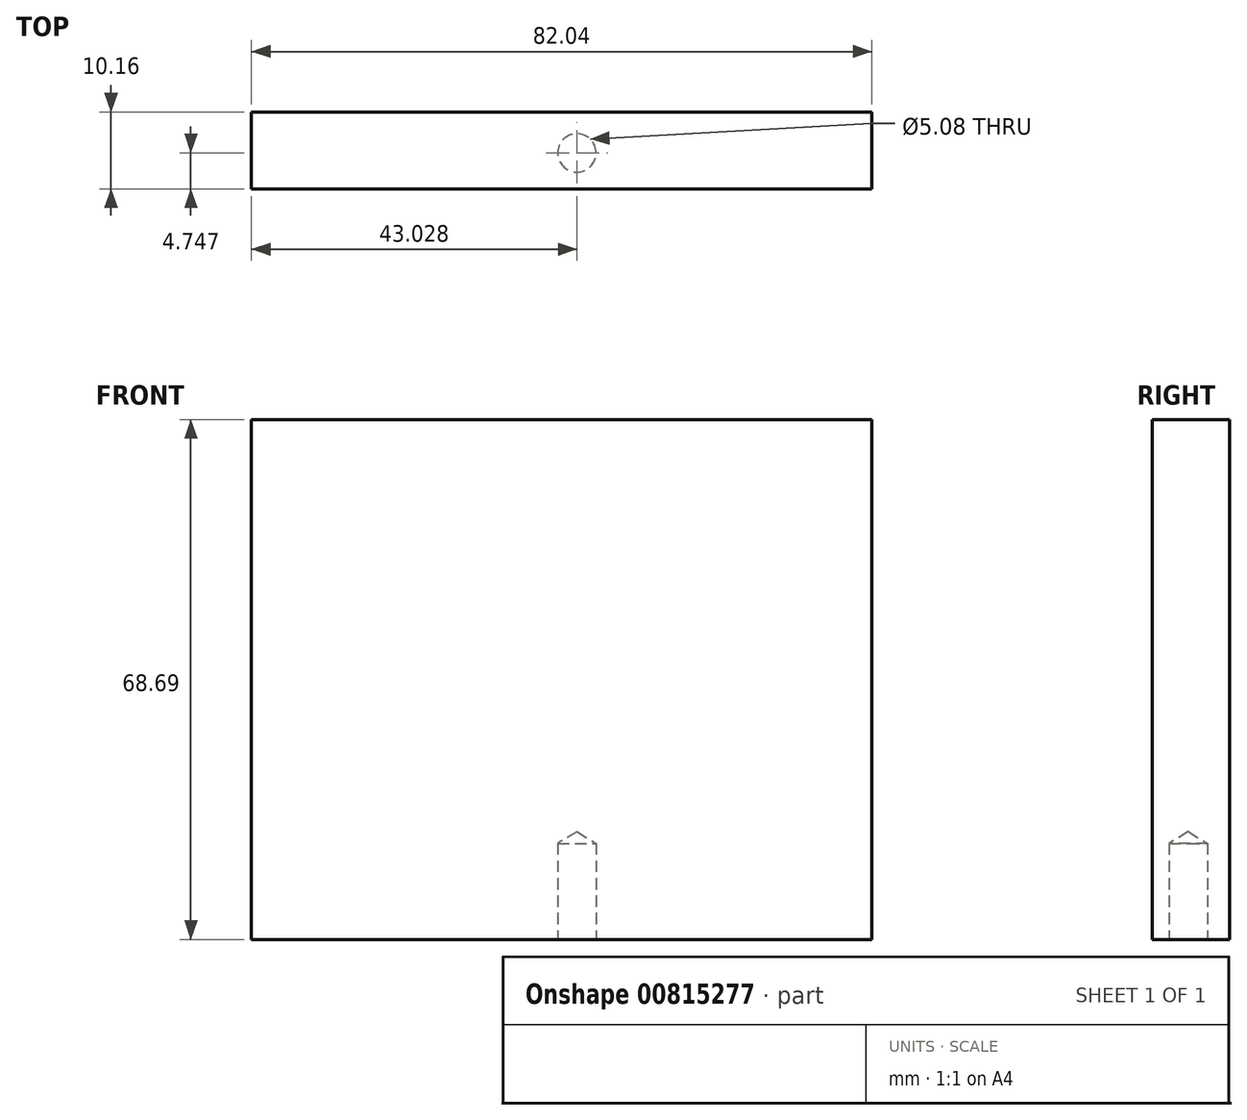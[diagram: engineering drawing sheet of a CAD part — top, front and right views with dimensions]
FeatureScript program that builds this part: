
annotation { "Feature Type Name" : "Feature", "Feature Type Description" : "" }
export const myFeature = defineFeature(function(context is Context, id is Id, definition is map)
    precondition{}
    {
        {
            var Q0;
            Q0=qCreatedBy(makeId("Front.planeOp"),FACE);
            var sketch = newSketch(context, id + "F0", { "sketchPlane" : qUnion([Q0])});
            skLineSegment(sketch, "E0.bottom", {"start": v(-60.47, 57.9) * mm, "end": v(21.57, 57.9) * mm});
            skLineSegment(sketch, "E0.top", {"start": v(-60.47, -10.79) * mm, "end": v(21.57, -10.79) * mm});
            skLineSegment(sketch, "E0.left", {"start": v(-60.47, 57.9) * mm, "end": v(-60.47, -10.79) * mm});
            skLineSegment(sketch, "E0.right", {"start": v(21.57, 57.9) * mm, "end": v(21.57, -10.79) * mm});
            skSolve(sketch);
        }
        {
            var Q0;
            Q0 = qSketchRegion(id + "F0", true);
            extrude(context, id + "F1", {"entities" : qUnion([Q0]), "depth" : 10.16 * mm, "offsetDistance" : 25.4 * mm});
        }
        {
            var Q0;
            Q0=makeQuery(id+"F1.opExtrude","SWEPT_FACE",FACE,{"disambiguationData":[OSD([sQuery(id+"F0.wireOp",EDGE,"E0.top")])]});
            var sketch = newSketch(context, id + "F2", { "sketchPlane" : qUnion([Q0])});
            skCircle(sketch, "E1", {"center": v(-17.44, 5.41) * mm, "radius": 2.54 * mm});
            skSolve(sketch);
        }
        {
            var Q0;
            Q0=sQuery(id+"F2.wireOp",VERTEX,"E1.center");
            var Q1;
            Q1=makeQuery(id+"F1.opExtrude","SWEPT_BODY",BODY,{"disambiguationData":[OSD([sQuery(id+"F0.wireOp",EDGE,"E0.bottom"),sQuery(id+"F0.wireOp",EDGE,"E0.top"),sQuery(id+"F0.wireOp",EDGE,"E0.left"),sQuery(id+"F0.wireOp",EDGE,"E0.right")])]});
            hole(context, id + "F3", {"style" : HoleStyle.SIMPLE, "endStyle" : HoleEndStyle.BLIND, "holeDiameter" : 5.08 * mm, "majorDiameter" : 6.35 * mm, "holeDepth" : 12.7 * mm, "isTappedThrough" : true, "tappedDepth" : 12.7 * mm, "tapClearance" : 3, "locations" : qUnion([Q0]), "scope" : qUnion([Q1])});
        }
    });
